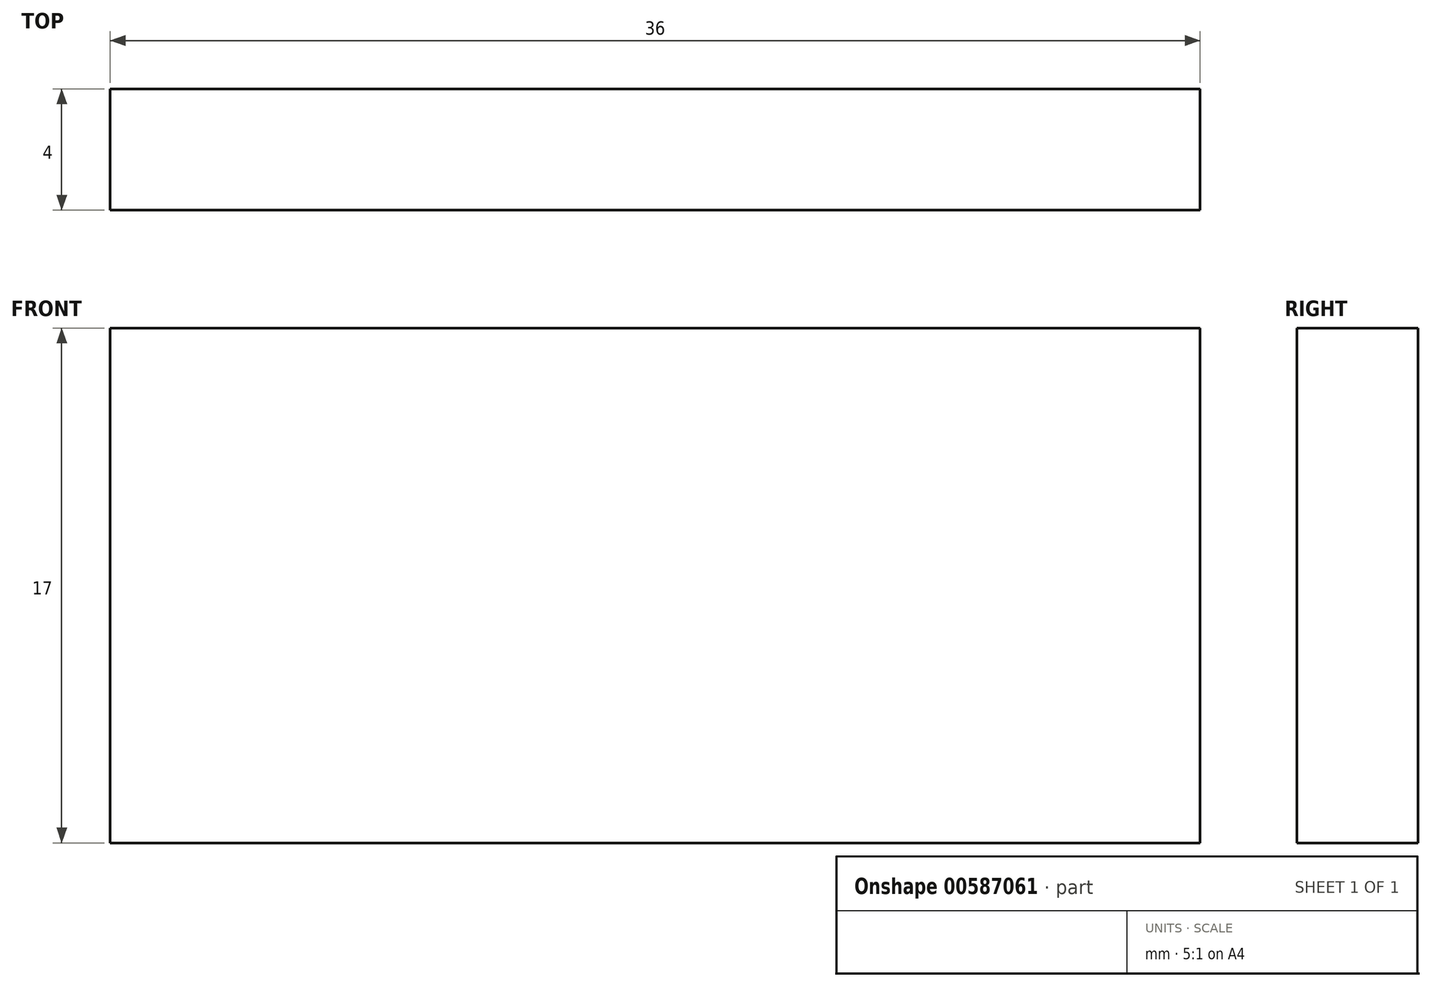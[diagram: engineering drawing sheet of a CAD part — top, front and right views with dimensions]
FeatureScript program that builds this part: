
annotation { "Feature Type Name" : "Feature", "Feature Type Description" : "" }
export const myFeature = defineFeature(function(context is Context, id is Id, definition is map)
    precondition{}
    {
        {
            var Q0;
            Q0=qCreatedBy(makeId("Front.planeOp"),FACE);
            var sketch = newSketch(context, id + "F0", { "sketchPlane" : qUnion([Q0])});
            skLineSegment(sketch, "E0.bottom", {"start": v(-18, 8.5) * mm, "end": v(18, 8.5) * mm});
            skLineSegment(sketch, "E0.top", {"start": v(-18, -8.5) * mm, "end": v(18, -8.5) * mm});
            skLineSegment(sketch, "E0.left", {"start": v(-18, 8.5) * mm, "end": v(-18, -8.5) * mm});
            skLineSegment(sketch, "E0.right", {"start": v(18, 8.5) * mm, "end": v(18, -8.5) * mm});
            skSolve(sketch);
        }
        {
            var Q0;
            Q0 = qSketchRegion(id + "F0", true);
            extrude(context, id + "F1", {"entities" : qUnion([Q0]), "depth" : 4 * mm});
        }
    });
